# Revit family: 1Plumbing-Fixture_Mincey-Marble-Manufacturing_CFP-Shower-Pan
name_source: partatom
category: Plumbing Fixtures
units: mm (PartAtom-declared; Revit-internal decimal feet)

## family parameters
Always vertical = Yes
Cut with Voids When Loaded = No
Maintain Annotation Orientation = No
OmniClass Number = 23.45.05.14.11.21
Part Type = Normal
Room Calculation Point = No
Round Connector Dimension = Use Diameter
Shared = No
Work Plane-Based = No

## types (3) — shared parameters
Assembly Code = D2010.60
Curb Offset = 4 "
Curve Offset = 30 "
Drain Diameter = 2 "
Floor Height = 1 "
Flow = 0 GPM
Height = 3 "
Keynote = 22 40 00.B3
Length = 60 "
Manufacturer = Mincey Marble Manufacturing
Product Documentation Link = https://minceymarble.com
Product Page URL = https://minceymarble.com
Short Side Depth = 30 "
URL = https://minceymarble.com
Vent Connection = No
Version = 1
zero-valued in all types: Default Elevation

## per-type parameters (varying)
| type | CFP | CFP-TD | Connector H Offset | Connector V Offset | Depth | Description | Drain H Offset | Drain V Offset | Model | Offset |
| CFP-TD-30-3460 - Shower Pan | No | Yes | 4 " | 14 " | 34 " | 30-34 x 60 Curved Front Trench Drain Shower Pan | 4 " | 14 " | CFP-TD-30-3460-OS-SF | 2 " |
| CFP-30-3460 - Shower Pan | Yes | No | 11 " | 18 " | 34 " | 30-34 x 60 Curved Front Renovation Shower Pan | 8 " | 15 " | CFP-30-3460-OS-SF-RENO | 3 " |
| CFP-30-3660 - Shower Pan | Yes | No | 10 " | 17 " | 36 " | 30-36 x 60 Curved Front Renovation Shower Pan | 9 " | 15 " | CFP-30-3660-OS-SF-RENO | 2 " |

## geometry (parser evidence)
native form markers: Sweep x2
no freeform markers — native parametric forms only
